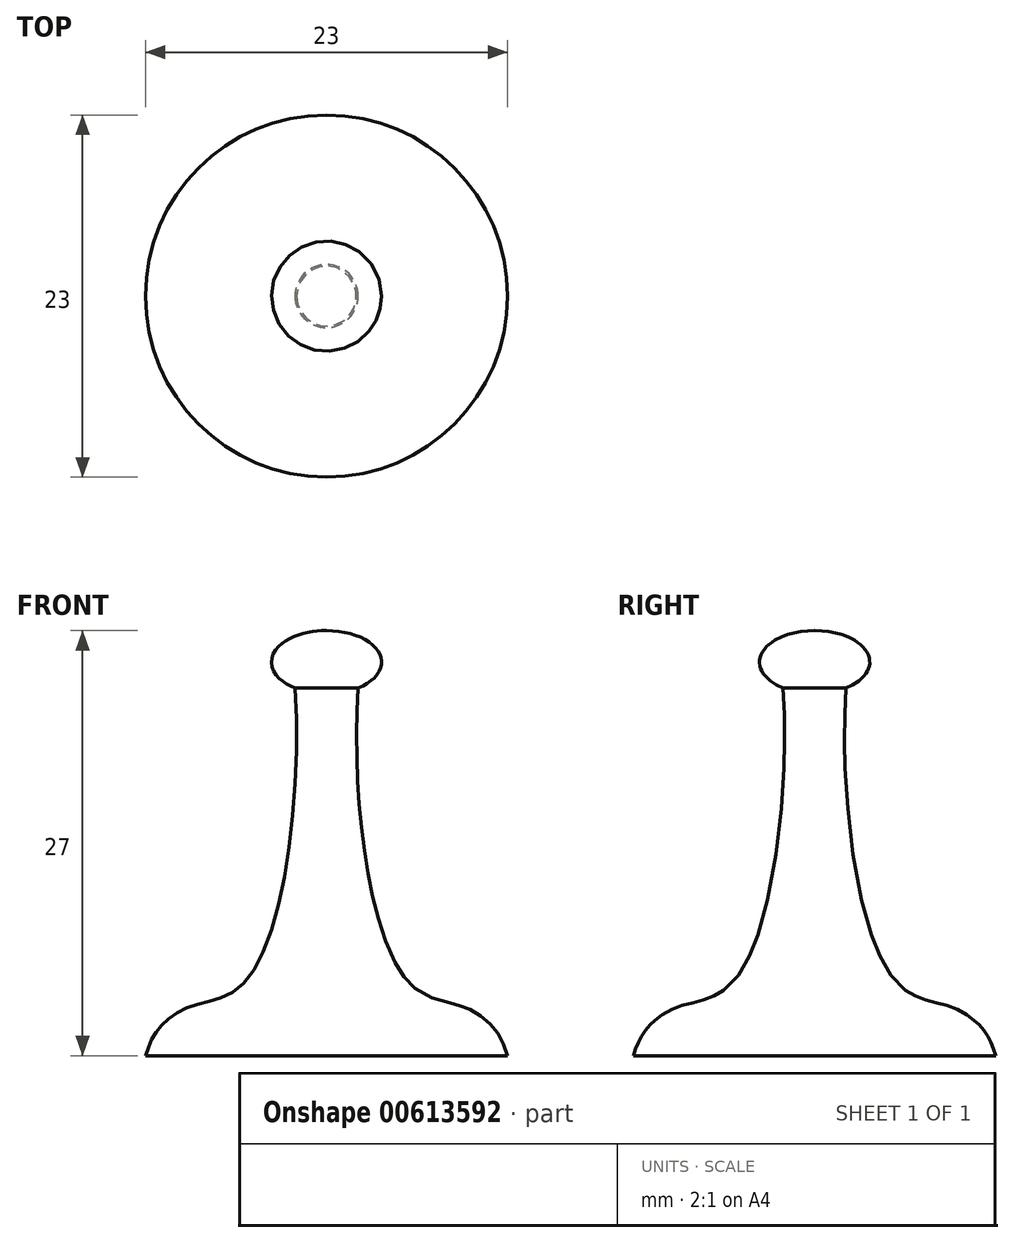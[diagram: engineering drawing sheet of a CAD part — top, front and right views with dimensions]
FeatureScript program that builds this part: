
annotation { "Feature Type Name" : "Feature", "Feature Type Description" : "" }
export const myFeature = defineFeature(function(context is Context, id is Id, definition is map)
    precondition{}
    {
        {
            var Q0;
            Q0=qCreatedBy(makeId("Front.planeOp"),FACE);
            var sketch = newSketch(context, id + "F0", { "sketchPlane" : qUnion([Q0])});
            skLineSegment(sketch, "E0", {"start": v(0, 0) * mm, "end": v(0, 27) * mm});
            skEllipticalArc(sketch, "E1", {});
            skLineSegment(sketch, "E2", {"start": v(0, 0) * mm, "end": v(11.5, 0) * mm});
            skLineSegment(sketch, "E3.0", {"start": v(2, 0) * mm, "end": v(2, 25) * mm, "construction": true});
            skFitSpline(sketch, "E4", {"points": [v(2, 23.36) * mm, v(5.13, 4.74) * mm, v(8.7, 3.1) * mm, v(10.7, 1.65) * mm, v(11.5, 0) * mm], "startDerivative": vector(-2.9, -44.3) * mm, "endDerivative": vector(3.99, -13.24) * mm});
            const initialGuessF0  = {"E1": [0, 0.025, 1, 0, 0.0035, 0.002, 5.3206345592948985, 1.5707963267948966]};
            skSetInitialGuess(sketch, initialGuessF0);
            skSolve(sketch);
        }
        {
            var Q0;
            Q0=makeQuery(id+"F0.imprint","IMPRINT",FACE,{"disambiguationData":[TD([[makeQuery(id+"F0.imprint","IMPRINT",EDGE,{"derivedFrom":sQuery(id+"F0.wireOp",EDGE,"E0")}),-1.0]])]});
            var Q1;
            Q1=sQuery(id+"F0.wireOp",EDGE,"E0");
            revolve(context, id + "F1", {"entities" : qUnion([Q0]), "axis" : qUnion([Q1]), "revolveType" : RevolveType.FULL});
        }
    });
